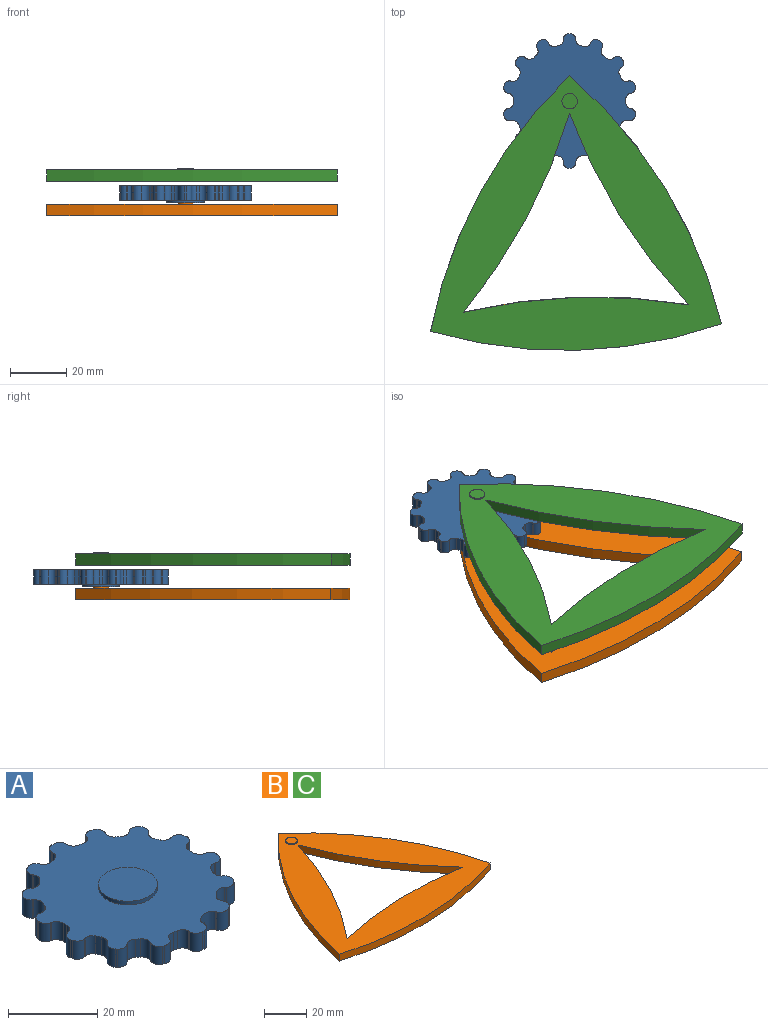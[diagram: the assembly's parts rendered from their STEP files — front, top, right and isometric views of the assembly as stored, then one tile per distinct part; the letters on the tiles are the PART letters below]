
ASSEMBLY  parts=3 mates=1
PART A: 116 faces, bbox 46.8x47.8x6 mm
  f0: cylinder r=20mm len=5mm, axis (0,0,-1), area 6.2mm2, adj f14,f15,f105,f113
  f1: cylinder r=20mm len=5mm, axis (0,0,-1), area 6.2mm2, adj f14,f15,f98,f106
  f2: cylinder r=20mm len=5mm, axis (0,0,-1), area 6.2mm2, adj f14,f15,f91,f99
  f3: cylinder r=20mm len=5mm, axis (0,0,-1), area 6.2mm2, adj f14,f15,f84,f92
  f4: cylinder r=20mm len=5mm, axis (0,0,-1), area 6.2mm2, adj f14,f15,f77,f85
  f5: cylinder r=20mm len=5mm, axis (0,0,-1), area 6.2mm2, adj f14,f15,f70,f78
  f6: cylinder r=20mm len=5mm, axis (0,0,-1), area 6.2mm2, adj f14,f15,f63,f71
  f7: cylinder r=20mm len=5mm, axis (0,0,-1), area 6.2mm2, adj f14,f15,f56,f64
  f8: cylinder r=20mm len=5mm, axis (0,0,-1), area 6.2mm2, adj f14,f15,f49,f57
  f9: cylinder r=20mm len=5mm, axis (0,0,-1), area 6.2mm2, adj f14,f15,f42,f50
  f10: cylinder r=20mm len=5mm, axis (0,0,-1), area 6.2mm2, adj f14,f15,f35,f43
  f11: cylinder r=20mm len=5mm, axis (0,0,-1), area 6.2mm2, adj f14,f15,f28,f36
  f12: cylinder r=20mm len=5mm, axis (0,0,-1), area 6.2mm2, adj f14,f15,f21,f29
  f13: cylinder r=20mm len=5mm, axis (0,0,-1), area 6.2mm2, adj f14,f15,f22,f112
  f14: plane 47.81x46.81mm, normal (0,0,1), area 1358.1mm2, adj f0,f1,f2,f3,f4,f5,f6,f7
  f15: plane 47.81x46.81mm, normal (0,0,-1), area 1495.4mm2, adj f0,f1,f2,f3,f4,f5,f6,f7
  f16: plane 5x0.31mm, normal (1,0,0), area 1.6mm2, adj f14,f15,f19,f22
  f17: plane 5x0.46mm, normal (0,1,0), area 2.3mm2, adj f14,f15,f19,f20
  f18: plane 5x0.31mm, normal (-1,0,0), area 1.6mm2, adj f14,f15,f20,f21
  f19: cylinder r=2mm len=5mm, axis (0,0,1), area 15.7mm2, adj f14,f15,f16,f17
  f20: cylinder r=2mm len=5mm, axis (0,0,-1), area 15.7mm2, adj f14,f15,f17,f18
  f21: cylinder r=2mm len=5mm, axis (0,0,-1), area 13.8mm2, adj f12,f14,f15,f18
  f22: cylinder r=2mm len=5mm, axis (0,0,-1), area 13.8mm2, adj f13,f14,f15,f16
  f23: plane 5x0.28mm, normal (0.9,0.43,0), area 1.6mm2, adj f14,f15,f26,f29
  f24: plane 5x0.42mm, normal (-0.43,0.9,0), area 2.3mm2, adj f14,f15,f26,f27
  f25: plane 5x0.28mm, normal (-0.9,-0.43,0), area 1.6mm2, adj f14,f15,f27,f28
  f26: cylinder r=2mm len=5mm, axis (0,0,1), area 15.7mm2, adj f14,f15,f23,f24
  f27: cylinder r=2mm len=5mm, axis (0,0,-1), area 15.7mm2, adj f14,f15,f24,f25
  f28: cylinder r=2mm len=5mm, axis (0,0,-1), area 13.8mm2, adj f11,f14,f15,f25
  f29: cylinder r=2mm len=5mm, axis (0,0,-1), area 13.8mm2, adj f12,f14,f15,f23
  f30: plane 5x0.24mm, normal (0.62,0.78,0), area 1.6mm2, adj f14,f15,f33,f36
  f31: plane 5x0.36mm, normal (-0.78,0.62,0), area 2.3mm2, adj f14,f15,f33,f34
  f32: plane 5x0.24mm, normal (-0.62,-0.78,0), area 1.6mm2, adj f14,f15,f34,f35
  f33: cylinder r=2mm len=5mm, axis (0,0,1), area 15.7mm2, adj f14,f15,f30,f31
  f34: cylinder r=2mm len=5mm, axis (0,0,-1), area 15.7mm2, adj f14,f15,f31,f32
  f35: cylinder r=2mm len=5mm, axis (0,0,-1), area 13.8mm2, adj f10,f14,f15,f32
  f36: cylinder r=2mm len=5mm, axis (0,0,-1), area 13.8mm2, adj f11,f14,f15,f30
  f37: plane 5x0.31mm, normal (0.22,0.97,0), area 1.6mm2, adj f14,f15,f40,f43
  f38: plane 5x0.45mm, normal (-0.97,0.22,0), area 2.3mm2, adj f14,f15,f40,f41
  f39: plane 5x0.31mm, normal (-0.22,-0.97,0), area 1.6mm2, adj f14,f15,f41,f42
  f40: cylinder r=2mm len=5mm, axis (0,0,1), area 15.7mm2, adj f14,f15,f37,f38
  f41: cylinder r=2mm len=5mm, axis (0,0,-1), area 15.7mm2, adj f14,f15,f38,f39
  f42: cylinder r=2mm len=5mm, axis (0,0,-1), area 13.8mm2, adj f9,f14,f15,f39
  f43: cylinder r=2mm len=5mm, axis (0,0,-1), area 13.8mm2, adj f10,f14,f15,f37
  f44: plane 5x0.31mm, normal (-0.22,0.97,0), area 1.6mm2, adj f14,f15,f47,f50
  f45: plane 5x0.45mm, normal (-0.97,-0.22,0), area 2.3mm2, adj f14,f15,f47,f48
  f46: plane 5x0.31mm, normal (0.22,-0.97,0), area 1.6mm2, adj f14,f15,f48,f49
  f47: cylinder r=2mm len=5mm, axis (0,0,1), area 15.7mm2, adj f14,f15,f44,f45
  f48: cylinder r=2mm len=5mm, axis (0,0,-1), area 15.7mm2, adj f14,f15,f45,f46
  f49: cylinder r=2mm len=5mm, axis (0,0,-1), area 13.8mm2, adj f8,f14,f15,f46
  f50: cylinder r=2mm len=5mm, axis (0,0,-1), area 13.8mm2, adj f9,f14,f15,f44
  f51: plane 5x0.24mm, normal (-0.62,0.78,0), area 1.6mm2, adj f14,f15,f54,f57
  f52: plane 5x0.36mm, normal (-0.78,-0.62,0), area 2.3mm2, adj f14,f15,f54,f55
  f53: plane 5x0.24mm, normal (0.62,-0.78,0), area 1.6mm2, adj f14,f15,f55,f56
  f54: cylinder r=2mm len=5mm, axis (0,0,1), area 15.7mm2, adj f14,f15,f51,f52
  f55: cylinder r=2mm len=5mm, axis (0,0,-1), area 15.7mm2, adj f14,f15,f52,f53
  f56: cylinder r=2mm len=5mm, axis (0,0,-1), area 13.8mm2, adj f7,f14,f15,f53
  f57: cylinder r=2mm len=5mm, axis (0,0,-1), area 13.8mm2, adj f8,f14,f15,f51
  f58: plane 5x0.28mm, normal (-0.9,0.43,0), area 1.6mm2, adj f14,f15,f61,f64
  f59: plane 5x0.42mm, normal (-0.43,-0.9,0), area 2.3mm2, adj f14,f15,f61,f62
  f60: plane 5x0.28mm, normal (0.9,-0.43,0), area 1.6mm2, adj f14,f15,f62,f63
  f61: cylinder r=2mm len=5mm, axis (0,0,1), area 15.7mm2, adj f14,f15,f58,f59
  f62: cylinder r=2mm len=5mm, axis (0,0,-1), area 15.7mm2, adj f14,f15,f59,f60
  f63: cylinder r=2mm len=5mm, axis (0,0,-1), area 13.8mm2, adj f6,f14,f15,f60
  f64: cylinder r=2mm len=5mm, axis (0,0,-1), area 13.8mm2, adj f7,f14,f15,f58
  f65: plane 5x0.31mm, normal (-1,0,0), area 1.6mm2, adj f14,f15,f68,f71
  f66: plane 5x0.46mm, normal (0,-1,0), area 2.3mm2, adj f14,f15,f68,f69
  f67: plane 5x0.31mm, normal (1,0,0), area 1.6mm2, adj f14,f15,f69,f70
  f68: cylinder r=2mm len=5mm, axis (0,0,1), area 15.7mm2, adj f14,f15,f65,f66
  f69: cylinder r=2mm len=5mm, axis (0,0,-1), area 15.7mm2, adj f14,f15,f66,f67
  f70: cylinder r=2mm len=5mm, axis (0,0,-1), area 13.8mm2, adj f5,f14,f15,f67
  f71: cylinder r=2mm len=5mm, axis (0,0,-1), area 13.8mm2, adj f6,f14,f15,f65
  f72: plane 5x0.28mm, normal (-0.9,-0.43,0), area 1.6mm2, adj f14,f15,f75,f78
  f73: plane 5x0.42mm, normal (0.43,-0.9,0), area 2.3mm2, adj f14,f15,f75,f76
  f74: plane 5x0.28mm, normal (0.9,0.43,0), area 1.6mm2, adj f14,f15,f76,f77
  f75: cylinder r=2mm len=5mm, axis (0,0,1), area 15.7mm2, adj f14,f15,f72,f73
  f76: cylinder r=2mm len=5mm, axis (0,0,-1), area 15.7mm2, adj f14,f15,f73,f74
  f77: cylinder r=2mm len=5mm, axis (0,0,-1), area 13.8mm2, adj f4,f14,f15,f74
  f78: cylinder r=2mm len=5mm, axis (0,0,-1), area 13.8mm2, adj f5,f14,f15,f72
  f79: plane 5x0.24mm, normal (-0.62,-0.78,0), area 1.6mm2, adj f14,f15,f82,f85
  f80: plane 5x0.36mm, normal (0.78,-0.62,0), area 2.3mm2, adj f14,f15,f82,f83
  f81: plane 5x0.24mm, normal (0.62,0.78,0), area 1.6mm2, adj f14,f15,f83,f84
  f82: cylinder r=2mm len=5mm, axis (0,0,1), area 15.7mm2, adj f14,f15,f79,f80
  f83: cylinder r=2mm len=5mm, axis (0,0,-1), area 15.7mm2, adj f14,f15,f80,f81
  f84: cylinder r=2mm len=5mm, axis (0,0,-1), area 13.8mm2, adj f3,f14,f15,f81
  f85: cylinder r=2mm len=5mm, axis (0,0,-1), area 13.8mm2, adj f4,f14,f15,f79
  f86: plane 5x0.31mm, normal (-0.22,-0.97,0), area 1.6mm2, adj f14,f15,f89,f92
  f87: plane 5x0.45mm, normal (0.97,-0.22,0), area 2.3mm2, adj f14,f15,f89,f90
  f88: plane 5x0.31mm, normal (0.22,0.97,0), area 1.6mm2, adj f14,f15,f90,f91
  f89: cylinder r=2mm len=5mm, axis (0,0,1), area 15.7mm2, adj f14,f15,f86,f87
  f90: cylinder r=2mm len=5mm, axis (0,0,-1), area 15.7mm2, adj f14,f15,f87,f88
  f91: cylinder r=2mm len=5mm, axis (0,0,-1), area 13.8mm2, adj f2,f14,f15,f88
  f92: cylinder r=2mm len=5mm, axis (0,0,-1), area 13.8mm2, adj f3,f14,f15,f86
  f93: plane 5x0.31mm, normal (0.22,-0.97,0), area 1.6mm2, adj f14,f15,f96,f99
  f94: plane 5x0.45mm, normal (0.97,0.22,0), area 2.3mm2, adj f14,f15,f96,f97
  f95: plane 5x0.31mm, normal (-0.22,0.97,0), area 1.6mm2, adj f14,f15,f97,f98
  f96: cylinder r=2mm len=5mm, axis (0,0,1), area 15.7mm2, adj f14,f15,f93,f94
  f97: cylinder r=2mm len=5mm, axis (0,0,-1), area 15.7mm2, adj f14,f15,f94,f95
  f98: cylinder r=2mm len=5mm, axis (0,0,-1), area 13.8mm2, adj f1,f14,f15,f95
  f99: cylinder r=2mm len=5mm, axis (0,0,-1), area 13.8mm2, adj f2,f14,f15,f93
  f100: plane 5x0.24mm, normal (0.62,-0.78,0), area 1.6mm2, adj f14,f15,f103,f106
  f101: plane 5x0.36mm, normal (0.78,0.62,0), area 2.3mm2, adj f14,f15,f103,f104
  f102: plane 5x0.24mm, normal (-0.62,0.78,0), area 1.6mm2, adj f14,f15,f104,f105
  f103: cylinder r=2mm len=5mm, axis (0,0,1), area 15.7mm2, adj f14,f15,f100,f101
  f104: cylinder r=2mm len=5mm, axis (0,0,-1), area 15.7mm2, adj f14,f15,f101,f102
  f105: cylinder r=2mm len=5mm, axis (0,0,-1), area 13.8mm2, adj f0,f14,f15,f102
  f106: cylinder r=2mm len=5mm, axis (0,0,-1), area 13.8mm2, adj f1,f14,f15,f100
  f107: plane 5x0.28mm, normal (0.9,-0.43,0), area 1.6mm2, adj f14,f15,f110,f113
  f108: plane 5x0.42mm, normal (0.43,0.9,0), area 2.3mm2, adj f14,f15,f110,f111
  f109: plane 5x0.28mm, normal (-0.9,0.43,0), area 1.6mm2, adj f14,f15,f111,f112
  f110: cylinder r=2mm len=5mm, axis (0,0,1), area 15.7mm2, adj f14,f15,f107,f108
  f111: cylinder r=2mm len=5mm, axis (0,0,-1), area 15.7mm2, adj f14,f15,f108,f109
  f112: cylinder r=2mm len=5mm, axis (0,0,-1), area 13.8mm2, adj f13,f14,f15,f109
  f113: cylinder r=2mm len=5mm, axis (0,0,-1), area 13.8mm2, adj f0,f14,f15,f107
  f114: cylinder r=6.61mm len=13.22mm, axis (0,0,-1), area 41.5mm2, adj f14,f115
  f115: plane 13.22x13.22mm, normal (0,0,1), area 137.4mm2, adj f114
PART B: 10 faces, bbox 103.4x97.7x4.5 mm
  f0: plane 103.39x97.68mm, normal (0,0,1), area 4154mm2, adj f2,f3,f4,f5,f6,f7,f8
  f1: plane 103.39x97.68mm, normal (0,0,-1), area 4177.5mm2, adj f2,f3,f4,f5,f6,f7
  f2: cylinder r=169.36mm len=103.39mm, axis (0,0,-1), area 420.4mm2, adj f0,f1,f3,f4
  f3: cylinder r=169.36mm len=88.22mm, axis (0,0,-1), area 420.4mm2, adj f0,f1,f2,f4
  f4: cylinder r=169.36mm len=90.86mm, axis (0,0,-1), area 420.4mm2, adj f0,f1,f2,f3
  f5: cylinder r=203.2mm len=70.59mm, axis (0,0,1), area 322.2mm2, adj f0,f1,f6,f7
  f6: cylinder r=203.2mm len=79.99mm, axis (0,0,1), area 322.2mm2, adj f0,f1,f5,f7
  f7: cylinder r=203.2mm len=67.95mm, axis (0,0,1), area 322.2mm2, adj f0,f1,f5,f6
  f8: cylinder r=2.74mm len=5.47mm, axis (0,0,-1), area 8.6mm2, adj f0,f9
  f9: plane 5.47x5.47mm, normal (0,0,1), area 23.5mm2, adj f8
PART C: same geometry as B
PLACE A rot(axis=(0,-1,0),180deg) t=(-6.54,74.75,4.97)mm
PLACE B t=(-6.54,25.39,-1.03)mm fixed
PLACE C t=(-6.54,25.27,11.19)mm
MATE fastened A.f114 <-> B.f8  axis (0,0,-1) through (-6.54,74.75,1.47)mm
